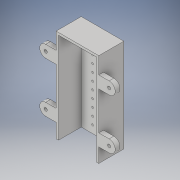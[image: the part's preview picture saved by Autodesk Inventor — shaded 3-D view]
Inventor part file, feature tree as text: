
AUTODESK INVENTOR PART (.ipt)
format: ipt  version: 2019.1 (Build 231200000, 200)  size: 207,872 bytes
history: native  units: in
note: dims shown in document units (in); Inventor stores cm internally (conversion verified against a paired STEP export)
features: sketch x5, extrude x4, mirror x2
ambient origin geometry x8: Origin, YZ Plane, XZ Plane, XY Plane, X Axis, Y Axis, Z Axis, Center Point
bodies: Solid1 (feature_tree)
feature tree (11):
  extrude  "Extrusion1"  Depth=0.1562in
  extrude  "Extrusion2"  Depth=1.5in
  extrude  "Extrusion4"  Depth=0.1562in
  mirror  "Mirror1"
  mirror  "Mirror2"
  extrude  "Extrusion5"  Depth=0.4in
  sketch  "Sketch7"  dims[d21=0.2in d22=0.3125in d23=0.0in d24=0.125in d25=0.75in d26=0.5in d27=4.3307in d29=0.5in d30=1.1811in d32=0.5in d35=1.0in d36=0.0in d37=1.25in d38=1.25in d39=0.1562in]
  sketch  "Sketch1"  dims[d2=0.1562in d3=0.1562in]
  sketch  "Sketch2"  dims[d6=6.0in d7=1.5in]
  sketch  "Sketch5"  dims[d8=0.0in d9=0.1562in]
  sketch  "Sketch6"  dims[d10=0.0in d18=0.4in]
